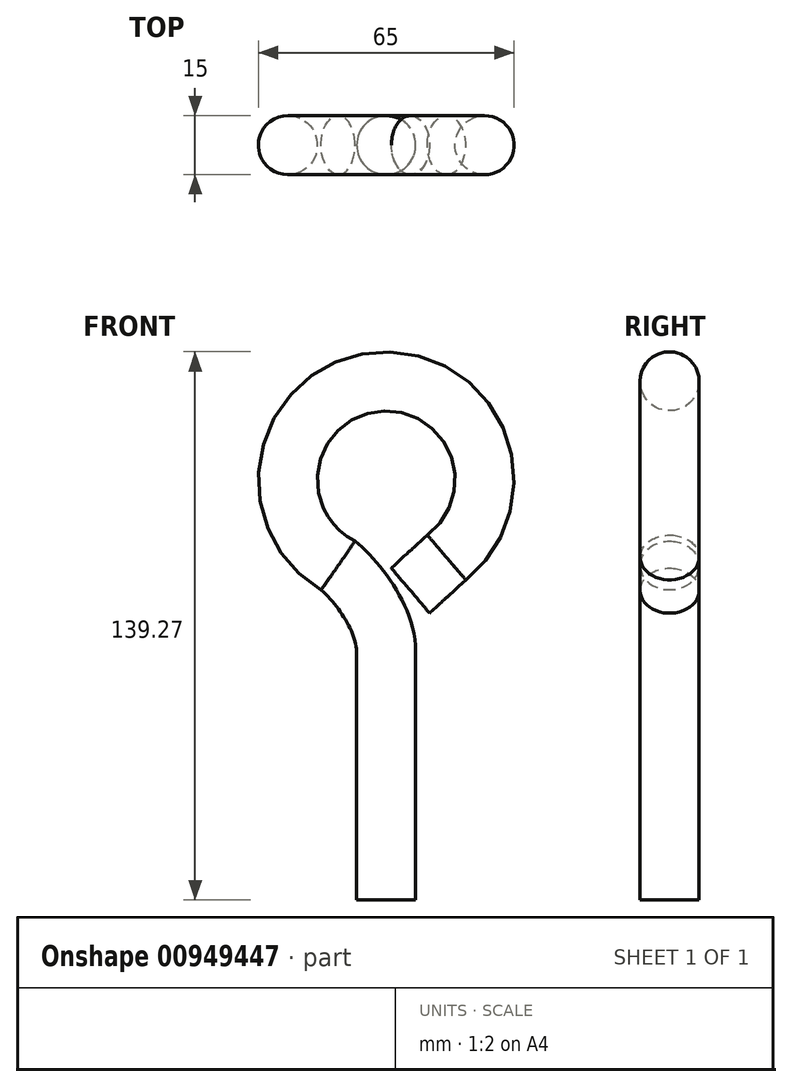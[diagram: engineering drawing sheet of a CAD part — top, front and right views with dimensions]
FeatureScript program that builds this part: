
annotation { "Feature Type Name" : "Feature", "Feature Type Description" : "" }
export const myFeature = defineFeature(function(context is Context, id is Id, definition is map)
    precondition{}
    {
        {
            var Q0;
            Q0=qCreatedBy(makeId("Front.planeOp"),FACE);
            var sketch = newSketch(context, id + "F0", { "sketchPlane" : qUnion([Q0])});
            skLineSegment(sketch, "E0", {"start": v(0, 0) * mm, "end": v(0, 63.05) * mm});
            skArc(sketch, "E1", {"start": v(15.32, 87.01) * mm, "mid": v(-1.87, 131.7) * mm, "end": v(-12.2, 84.95) * mm});
            skFitSpline(sketch, "E2", {"points": [v(0, 63.05) * mm, v(-12.2, 84.95) * mm], "startDerivative": vector(0, 23.23) * mm, "endDerivative": vector(-16.98, 14.23) * mm});
            skFitSpline(sketch, "E3", {"points": [v(15.32, 87.01) * mm, v(9.64, 81.83) * mm, v(6.17, 78.57) * mm], "startDerivative": vector(-21.65, -20.6) * mm, "endDerivative": vector(-5.14, -4.36) * mm});
            skSolve(sketch);
        }
        {
            var Q0;
            Q0=qCreatedBy(makeId("Top.planeOp"),FACE);
            var sketch = newSketch(context, id + "F1", { "sketchPlane" : qUnion([Q0])});
            skCircle(sketch, "E4", {"center": v(0, 0) * mm, "radius": 7.5 * mm});
            skSolve(sketch);
        }
        {
            var Q0;
            Q0=makeQuery(id+"F1.imprint","IMPRINT",FACE,{"disambiguationData":[TD([[makeQuery(id+"F1.imprint","IMPRINT",EDGE,{"derivedFrom":sQuery(id+"F1.wireOp",EDGE,"E4")}),1.0]])]});
            var Q1;
            Q1=sQuery(id+"F0.wireOp",EDGE,"E0");
            var Q2;
            Q2=sQuery(id+"F0.wireOp",EDGE,"E2");
            var Q3;
            Q3=sQuery(id+"F0.wireOp",EDGE,"E1");
            var Q4;
            Q4=sQuery(id+"F0.wireOp",EDGE,"E3");
            sweep(context, id + "F2", {"profiles" : qUnion([Q0]), "path" : qUnion([Q1, Q2, Q3, Q4])});
        }
    });
